# Revit family: Building-Materials_Glass-Glazing_Vitro-Architectural-Glass_SOLARBAN-R100
name_source: partatom
category: Curtain Panels
units: mm (PartAtom-declared; Revit-internal decimal feet)

## family parameters
Always vertical = Yes
Classification Number = 23.25.20.14.11.11.17
Cut with Voids When Loaded = No
Shared = No

## types (3) — shared parameters
1st Lite Thickness = 0' - 0 1/4"
2nd Lite Thickness = 0' - 0 1/4"
Airspace Thickness = 0' - 0 1/2"
Analytic Construction = Low-E double glazing (1/4 in + 1/4 in)
Assembly Code = B2020220
Define Thermal Properties by = Schematic Type
Description = Solarban® R100 glass is a neutral-reflective low‑e glass with an excellent solar heat gain coefficient (SHGC).
Finish = Glass
Heat Transfer Coefficient (U) = 0.29 BTU/(h·ft²·°F)
Keynote = 08900
Manufacturer = Vitro Architectural Glass
Product Guid = 883c3035-ad6e-49f1-9eb2-5b4d049a876f
Product Page URL = https://www.vitroglazings.com
Product data url = https://www.bimobject.com
Shadow Coefficient = 0.27
Solar Heat Gain Coefficient = 0.23
Thermal Resistance (R) = 8.3333 (h·ft²·°F)/BTU
Total Thickness = 0' - 1"
U-Value Air (Summer Day) = 0.27 BTU/(h·ft²·°F)
U-Value Air (Winter Night) = 0.29 BTU/(h·ft²·°F)
U-Value Argon (Summer Day) = 0.22 BTU/(h·ft²·°F)
U-Value Argon (Winter Night) = 0.25 BTU/(h·ft²·°F)
URL = https://www.vitroglazings.com

## per-type parameters (varying)
| type | Exterior Glass Material | Glass Code | ISO Damage Weighted Transmittance | Interior Glass Material | Light to Solar Gain | Reflectance (Visible Exterior) | Reflectance (Visible Interior) | Solar Light Transmittance | UV Light Transmittance | Visual Light Transmittance |
| Solarban R100 (2) Clear + Clear | Vitro Architectural-Glass - Solarban R100 (2) Clear | 1 | 0.336 | Vitro Architectural-Glass - Clear | 1.83 | 32 | 14 | 0.19 | 0.12 | 0.42 |
| Solarban R100 (2) Starphire + Starphire | Vitro Architectural-Glass - Solarban R100 (2) Starphire | 2 | 0.366 | Vitro Architectural-Glass - Starphire | 1.91 | 33 | 14 | 0.21 | 0.16 | 0.44 |
| Solarban R100 (2) Acuity + Acuity | Vitro Architectural-Glass - Solarban R100 (2) Acuity | 3 | 0.356 | Vitro Architectural-Glass - Acuity | 1.87 | 33 | 13 | 0.21 | 0.14 | 0.43 |

note: column(s) folded — value = type name in every type: Model

## geometry (parser evidence)
native form markers: Sweep x2
no freeform markers — native parametric forms only
